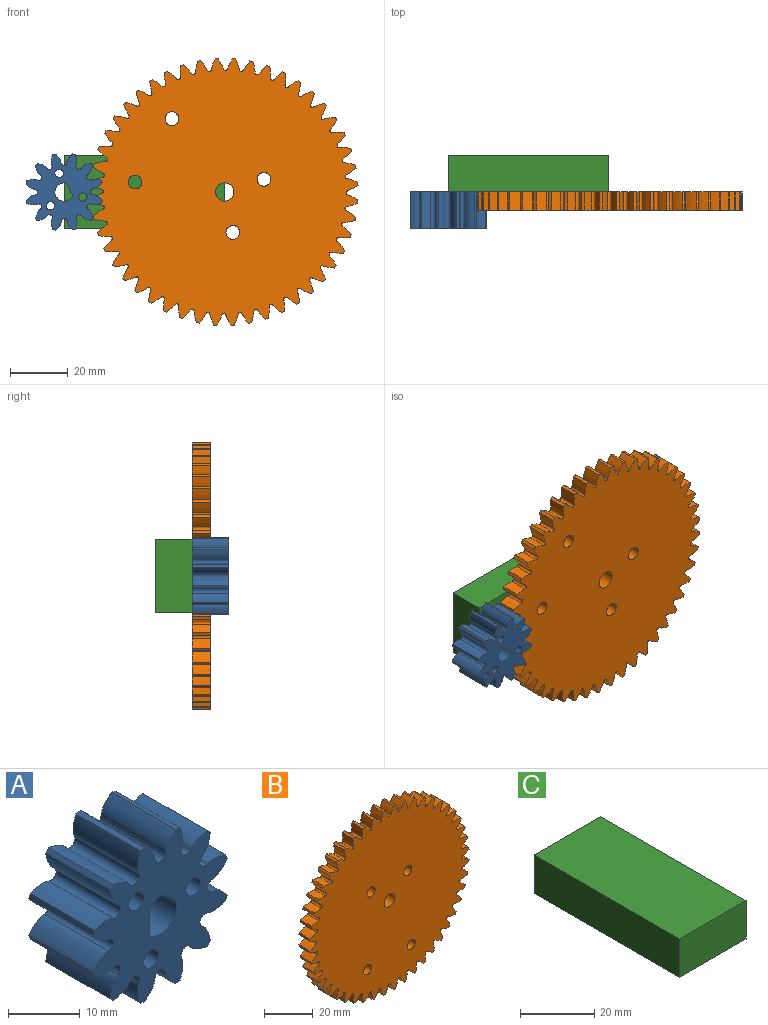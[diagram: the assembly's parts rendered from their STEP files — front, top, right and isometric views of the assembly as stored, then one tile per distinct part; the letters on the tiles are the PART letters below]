
ASSEMBLY  parts=3 mates=2
PART A: 55 faces, bbox 26.4x12.7x26.4 mm
  f0: cylinder r=13.54mm len=12.7mm, axis (0,1,0), area 10.8mm2, adj f11,f12,f41,f48
  f1: cylinder r=13.54mm len=12.7mm, axis (0,1,0), area 10.8mm2, adj f11,f12,f45,f47
  f2: cylinder r=13.54mm len=12.7mm, axis (0,1,0), area 10.8mm2, adj f11,f12,f38,f42
  f3: cylinder r=13.54mm len=12.7mm, axis (0,1,0), area 10.8mm2, adj f11,f12,f35,f39
  f4: cylinder r=13.54mm len=12.7mm, axis (0,1,0), area 10.8mm2, adj f11,f12,f32,f36
  f5: cylinder r=13.54mm len=12.7mm, axis (0,1,0), area 10.8mm2, adj f11,f12,f26,f33
  f6: cylinder r=13.54mm len=12.7mm, axis (0,1,0), area 10.8mm2, adj f11,f12,f14,f30
  f7: cylinder r=13.54mm len=12.7mm, axis (0,1,0), area 10.8mm2, adj f11,f12,f27,f29
  f8: cylinder r=13.54mm len=12.7mm, axis (0,1,0), area 10.8mm2, adj f11,f12,f20,f24
  f9: cylinder r=13.54mm len=12.7mm, axis (0,1,0), area 10.8mm2, adj f11,f12,f17,f21
  f10: cylinder r=13.54mm len=12.7mm, axis (0,1,0), area 10.8mm2, adj f11,f12,f18,f44
  f11: plane 26.38x26.38mm, normal (0,-1,0), area 363.7mm2, adj f0,f1,f2,f3,f4,f5,f6,f7
  f12: plane 26.38x26.38mm, normal (0,1,0), area 363.7mm2, adj f0,f1,f2,f3,f4,f5,f6,f7
  f13: cylinder r=13.54mm len=12.7mm, axis (0,1,0), area 10.8mm2, adj f11,f12,f15,f23
  f14: extruded ~12.7x3.07mm, area 48.5mm2, adj f6,f11,f12,f16
  f15: extruded ~12.7x3.07mm, area 48.5mm2, adj f11,f12,f13,f16
  f16: cylinder r=1.03mm len=12.7mm, axis (0,1,0), area 38.3mm2, adj f11,f12,f14,f15
  f17: extruded ~12.7x3.07mm, area 48.5mm2, adj f9,f11,f12,f19
  f18: extruded ~12.7x3.07mm, area 48.5mm2, adj f10,f11,f12,f19
  f19: cylinder r=1.03mm len=12.7mm, axis (0,1,0), area 38.3mm2, adj f11,f12,f17,f18
  f20: extruded ~12.7x3.33mm, area 48.5mm2, adj f8,f11,f12,f22
  f21: extruded ~12.7x3.69mm, area 48.5mm2, adj f9,f11,f12,f22
  f22: cylinder r=1.03mm len=12.7mm, axis (0,1,0), area 38.3mm2, adj f11,f12,f20,f21
  f23: extruded ~12.7x3.69mm, area 48.5mm2, adj f11,f12,f13,f25
  f24: extruded ~12.7x3.33mm, area 48.5mm2, adj f8,f11,f12,f25
  f25: cylinder r=1.03mm len=12.7mm, axis (0,1,0), area 38.3mm2, adj f11,f12,f23,f24
  f26: extruded ~12.7x3.69mm, area 48.5mm2, adj f5,f11,f12,f28
  f27: extruded ~12.7x3.33mm, area 48.5mm2, adj f7,f11,f12,f28
  f28: cylinder r=1.03mm len=12.7mm, axis (0,1,0), area 38.3mm2, adj f11,f12,f26,f27
  f29: extruded ~12.7x3.33mm, area 48.5mm2, adj f7,f11,f12,f31
  f30: extruded ~12.7x3.69mm, area 48.5mm2, adj f6,f11,f12,f31
  f31: cylinder r=1.03mm len=12.7mm, axis (0,1,0), area 38.3mm2, adj f11,f12,f29,f30
  f32: extruded ~12.7x3.07mm, area 48.5mm2, adj f4,f11,f12,f34
  f33: extruded ~12.7x3.07mm, area 48.5mm2, adj f5,f11,f12,f34
  f34: cylinder r=1.03mm len=12.7mm, axis (0,1,0), area 38.3mm2, adj f11,f12,f32,f33
  f35: extruded ~12.7x3.33mm, area 48.5mm2, adj f3,f11,f12,f37
  f36: extruded ~12.7x3.69mm, area 48.5mm2, adj f4,f11,f12,f37
  f37: cylinder r=1.03mm len=12.7mm, axis (0,1,0), area 38.3mm2, adj f11,f12,f35,f36
  f38: extruded ~12.7x3.69mm, area 48.5mm2, adj f2,f11,f12,f40
  f39: extruded ~12.7x3.33mm, area 48.5mm2, adj f3,f11,f12,f40
  f40: cylinder r=1.03mm len=12.7mm, axis (0,1,0), area 38.3mm2, adj f11,f12,f38,f39
  f41: extruded ~12.7x3.07mm, area 48.5mm2, adj f0,f11,f12,f43
  f42: extruded ~12.7x3.07mm, area 48.5mm2, adj f2,f11,f12,f43
  f43: cylinder r=1.03mm len=12.7mm, axis (0,1,0), area 38.3mm2, adj f11,f12,f41,f42
  f44: extruded ~12.7x3.69mm, area 48.5mm2, adj f10,f11,f12,f46
  f45: extruded ~12.7x3.33mm, area 48.5mm2, adj f1,f11,f12,f46
  f46: cylinder r=1.03mm len=12.7mm, axis (0,1,0), area 38.3mm2, adj f11,f12,f44,f45
  f47: extruded ~12.7x3.33mm, area 48.5mm2, adj f1,f11,f12,f49
  f48: extruded ~12.7x3.69mm, area 48.5mm2, adj f0,f11,f12,f49
  f49: cylinder r=1.03mm len=12.7mm, axis (0,1,0), area 38.3mm2, adj f11,f12,f47,f48
  f50: cylinder r=1.46mm len=12.7mm, axis (0,-1,0), area 116.5mm2, adj f11,f12
  f51: cylinder r=1.46mm len=12.7mm, axis (0,-1,0), area 116.5mm2, adj f11,f12
  f52: cylinder r=3.17mm len=12.7mm, axis (0,-1,0), area 183.5mm2, adj f11,f12,f53
  f53: plane 12.7x4.84mm, normal (1,0,0), area 61.4mm2, adj f11,f12,f52
  f54: cylinder r=1.46mm len=12.7mm, axis (0,-1,0), area 116.5mm2, adj f11,f12
PART B: 199 faces, bbox 92.4x6.4x92.4 mm
  f0: cylinder r=46.25mm len=6.35mm, axis (0,1,0), area 6.8mm2, adj f47,f48,f188,f192
  f1: cylinder r=46.25mm len=6.35mm, axis (0,1,0), area 6.8mm2, adj f47,f48,f179,f189
  f2: cylinder r=46.25mm len=6.35mm, axis (0,1,0), area 6.8mm2, adj f47,f48,f186,f191
  f3: cylinder r=46.25mm len=6.35mm, axis (0,1,0), area 6.8mm2, adj f47,f48,f183,f185
  f4: cylinder r=46.25mm len=6.35mm, axis (0,1,0), area 6.8mm2, adj f47,f48,f176,f180
  f5: cylinder r=46.25mm len=6.35mm, axis (0,1,0), area 6.8mm2, adj f47,f48,f173,f177
  f6: cylinder r=46.25mm len=6.35mm, axis (0,1,0), area 6.8mm2, adj f47,f48,f170,f174
  f7: cylinder r=46.25mm len=6.35mm, axis (0,1,0), area 6.8mm2, adj f47,f48,f167,f171
  f8: cylinder r=46.25mm len=6.35mm, axis (0,1,0), area 6.8mm2, adj f47,f48,f164,f168
  f9: cylinder r=46.25mm len=6.35mm, axis (0,1,0), area 6.8mm2, adj f47,f48,f161,f165
  f10: cylinder r=46.25mm len=6.35mm, axis (0,1,0), area 6.8mm2, adj f47,f48,f158,f162
  f11: cylinder r=46.25mm len=6.35mm, axis (0,1,0), area 6.8mm2, adj f47,f48,f146,f159
  f12: cylinder r=46.25mm len=6.35mm, axis (0,1,0), area 6.8mm2, adj f47,f48,f152,f156
  f13: cylinder r=46.25mm len=6.35mm, axis (0,1,0), area 6.8mm2, adj f47,f48,f143,f153
  f14: cylinder r=46.25mm len=6.35mm, axis (0,1,0), area 6.8mm2, adj f47,f48,f150,f155
  f15: cylinder r=46.25mm len=6.35mm, axis (0,1,0), area 6.8mm2, adj f47,f48,f147,f149
  f16: cylinder r=46.25mm len=6.35mm, axis (0,1,0), area 6.8mm2, adj f47,f48,f140,f144
  f17: cylinder r=46.25mm len=6.35mm, axis (0,1,0), area 6.8mm2, adj f47,f48,f137,f141
  f18: cylinder r=46.25mm len=6.35mm, axis (0,1,0), area 6.8mm2, adj f47,f48,f134,f138
  f19: cylinder r=46.25mm len=6.35mm, axis (0,1,0), area 6.8mm2, adj f47,f48,f131,f135
  f20: cylinder r=46.25mm len=6.35mm, axis (0,1,0), area 6.8mm2, adj f47,f48,f128,f132
  f21: cylinder r=46.25mm len=6.35mm, axis (0,1,0), area 6.8mm2, adj f47,f48,f125,f129
  f22: cylinder r=46.25mm len=6.35mm, axis (0,1,0), area 6.8mm2, adj f47,f48,f122,f126
  f23: cylinder r=46.25mm len=6.35mm, axis (0,1,0), area 6.8mm2, adj f47,f48,f110,f123
  f24: cylinder r=46.25mm len=6.35mm, axis (0,1,0), area 6.8mm2, adj f47,f48,f116,f120
  f25: cylinder r=46.25mm len=6.35mm, axis (0,1,0), area 6.8mm2, adj f47,f48,f107,f117
  f26: cylinder r=46.25mm len=6.35mm, axis (0,1,0), area 6.8mm2, adj f47,f48,f114,f119
  f27: cylinder r=46.25mm len=6.35mm, axis (0,1,0), area 6.8mm2, adj f47,f48,f111,f113
  f28: cylinder r=46.25mm len=6.35mm, axis (0,1,0), area 6.8mm2, adj f47,f48,f104,f108
  f29: cylinder r=46.25mm len=6.35mm, axis (0,1,0), area 6.8mm2, adj f47,f48,f101,f105
  f30: cylinder r=46.25mm len=6.35mm, axis (0,1,0), area 6.8mm2, adj f47,f48,f98,f102
  f31: cylinder r=46.25mm len=6.35mm, axis (0,1,0), area 6.8mm2, adj f47,f48,f50,f99
  f32: cylinder r=46.25mm len=6.35mm, axis (0,1,0), area 6.8mm2, adj f47,f48,f96,f182
  f33: cylinder r=46.25mm len=6.35mm, axis (0,1,0), area 6.8mm2, adj f47,f48,f93,f95
  f34: cylinder r=46.25mm len=6.35mm, axis (0,1,0), area 6.8mm2, adj f47,f48,f90,f92
  f35: cylinder r=46.25mm len=6.35mm, axis (0,1,0), area 6.8mm2, adj f47,f48,f87,f89
  f36: cylinder r=46.25mm len=6.35mm, axis (0,1,0), area 6.8mm2, adj f47,f48,f84,f86
  f37: cylinder r=46.25mm len=6.35mm, axis (0,1,0), area 6.8mm2, adj f47,f48,f81,f83
  f38: cylinder r=46.25mm len=6.35mm, axis (0,1,0), area 6.8mm2, adj f47,f48,f78,f80
  f39: cylinder r=46.25mm len=6.35mm, axis (0,1,0), area 6.8mm2, adj f47,f48,f75,f77
  f40: cylinder r=46.25mm len=6.35mm, axis (0,1,0), area 6.8mm2, adj f47,f48,f68,f72
  f41: cylinder r=46.25mm len=6.35mm, axis (0,1,0), area 6.8mm2, adj f47,f48,f62,f69
  f42: cylinder r=46.25mm len=6.35mm, axis (0,1,0), area 6.8mm2, adj f47,f48,f66,f74
  f43: cylinder r=46.25mm len=6.35mm, axis (0,1,0), area 6.8mm2, adj f47,f48,f63,f65
  f44: cylinder r=46.25mm len=6.35mm, axis (0,1,0), area 6.8mm2, adj f47,f48,f60,f71
  f45: cylinder r=46.25mm len=6.35mm, axis (0,1,0), area 6.8mm2, adj f47,f48,f57,f59
  f46: cylinder r=46.25mm len=6.35mm, axis (0,1,0), area 6.8mm2, adj f47,f48,f54,f56
  f47: plane 92.36x92.36mm, normal (0,-1,0), area 6064.5mm2, adj f0,f1,f2,f3,f4,f5,f6,f7
  f48: plane 92.36x92.36mm, normal (0,1,0), area 6064.5mm2, adj f0,f1,f2,f3,f4,f5,f6,f7
  f49: cylinder r=46.25mm len=6.35mm, axis (0,1,0), area 6.8mm2, adj f47,f48,f51,f53
  f50: extruded ~6.35x3.63mm, area 25.9mm2, adj f31,f47,f48,f52
  f51: extruded ~6.35x3.63mm, area 25.9mm2, adj f47,f48,f49,f52
  f52: cylinder r=0.7mm len=6.35mm, axis (0,1,0), area 10.8mm2, adj f47,f48,f50,f51
  f53: extruded ~6.35x3.84mm, area 25.9mm2, adj f47,f48,f49,f55
  f54: extruded ~6.35x3.36mm, area 25.9mm2, adj f46,f47,f48,f55
  f55: cylinder r=0.7mm len=6.35mm, axis (0,1,0), area 10.8mm2, adj f47,f48,f53,f54
  f56: extruded ~6.35x3.99mm, area 25.9mm2, adj f46,f47,f48,f58
  f57: extruded ~6.35x3.04mm, area 25.9mm2, adj f45,f47,f48,f58
  f58: cylinder r=0.7mm len=6.35mm, axis (0,1,0), area 10.8mm2, adj f47,f48,f56,f57
  f59: extruded ~6.35x4.06mm, area 25.9mm2, adj f45,f47,f48,f61
  f60: extruded ~6.35x3.09mm, area 25.9mm2, adj f44,f47,f48,f61
  f61: cylinder r=0.7mm len=6.35mm, axis (0,1,0), area 10.8mm2, adj f47,f48,f59,f60
  f62: extruded ~6.35x3.87mm, area 25.9mm2, adj f41,f47,f48,f64
  f63: extruded ~6.35x3.87mm, area 25.9mm2, adj f43,f47,f48,f64
  f64: cylinder r=0.7mm len=6.35mm, axis (0,1,0), area 10.8mm2, adj f47,f48,f62,f63
  f65: extruded ~6.35x3.67mm, area 25.9mm2, adj f43,f47,f48,f67
  f66: extruded ~6.35x4mm, area 25.9mm2, adj f42,f47,f48,f67
  f67: cylinder r=0.7mm len=6.35mm, axis (0,1,0), area 10.8mm2, adj f47,f48,f65,f66
  f68: extruded ~6.35x4mm, area 25.9mm2, adj f40,f47,f48,f70
  f69: extruded ~6.35x3.67mm, area 25.9mm2, adj f41,f47,f48,f70
  f70: cylinder r=0.7mm len=6.35mm, axis (0,1,0), area 10.8mm2, adj f47,f48,f68,f69
  f71: extruded ~6.35x4.07mm, area 25.9mm2, adj f44,f47,f48,f73
  f72: extruded ~6.35x3.41mm, area 25.9mm2, adj f40,f47,f48,f73
  f73: cylinder r=0.7mm len=6.35mm, axis (0,1,0), area 10.8mm2, adj f47,f48,f71,f72
  f74: extruded ~6.35x3.41mm, area 25.9mm2, adj f42,f47,f48,f76
  f75: extruded ~6.35x4.07mm, area 25.9mm2, adj f39,f47,f48,f76
  f76: cylinder r=0.7mm len=6.35mm, axis (0,1,0), area 10.8mm2, adj f47,f48,f74,f75
  f77: extruded ~6.35x3.09mm, area 25.9mm2, adj f39,f47,f48,f79
  f78: extruded ~6.35x4.06mm, area 25.9mm2, adj f38,f47,f48,f79
  f79: cylinder r=0.7mm len=6.35mm, axis (0,1,0), area 10.8mm2, adj f47,f48,f77,f78
  f80: extruded ~6.35x3.04mm, area 25.9mm2, adj f38,f47,f48,f82
  f81: extruded ~6.35x3.99mm, area 25.9mm2, adj f37,f47,f48,f82
  f82: cylinder r=0.7mm len=6.35mm, axis (0,1,0), area 10.8mm2, adj f47,f48,f80,f81
  f83: extruded ~6.35x3.36mm, area 25.9mm2, adj f37,f47,f48,f85
  f84: extruded ~6.35x3.84mm, area 25.9mm2, adj f36,f47,f48,f85
  f85: cylinder r=0.7mm len=6.35mm, axis (0,1,0), area 10.8mm2, adj f47,f48,f83,f84
  f86: extruded ~6.35x3.63mm, area 25.9mm2, adj f36,f47,f48,f88
  f87: extruded ~6.35x3.63mm, area 25.9mm2, adj f35,f47,f48,f88
  f88: cylinder r=0.7mm len=6.35mm, axis (0,1,0), area 10.8mm2, adj f47,f48,f86,f87
  f89: extruded ~6.35x3.84mm, area 25.9mm2, adj f35,f47,f48,f91
  f90: extruded ~6.35x3.36mm, area 25.9mm2, adj f34,f47,f48,f91
  f91: cylinder r=0.7mm len=6.35mm, axis (0,1,0), area 10.8mm2, adj f47,f48,f89,f90
  f92: extruded ~6.35x3.99mm, area 25.9mm2, adj f34,f47,f48,f94
  f93: extruded ~6.35x3.04mm, area 25.9mm2, adj f33,f47,f48,f94
  f94: cylinder r=0.7mm len=6.35mm, axis (0,1,0), area 10.8mm2, adj f47,f48,f92,f93
  f95: extruded ~6.35x4.06mm, area 25.9mm2, adj f33,f47,f48,f97
  f96: extruded ~6.35x3.09mm, area 25.9mm2, adj f32,f47,f48,f97
  f97: cylinder r=0.7mm len=6.35mm, axis (0,1,0), area 10.8mm2, adj f47,f48,f95,f96
  f98: extruded ~6.35x3.36mm, area 25.9mm2, adj f30,f47,f48,f100
  f99: extruded ~6.35x3.84mm, area 25.9mm2, adj f31,f47,f48,f100
  f100: cylinder r=0.7mm len=6.35mm, axis (0,1,0), area 10.8mm2, adj f47,f48,f98,f99
  f101: extruded ~6.35x3.04mm, area 25.9mm2, adj f29,f47,f48,f103
  f102: extruded ~6.35x3.99mm, area 25.9mm2, adj f30,f47,f48,f103
  f103: cylinder r=0.7mm len=6.35mm, axis (0,1,0), area 10.8mm2, adj f47,f48,f101,f102
  f104: extruded ~6.35x3.09mm, area 25.9mm2, adj f28,f47,f48,f106
  f105: extruded ~6.35x4.06mm, area 25.9mm2, adj f29,f47,f48,f106
  f106: cylinder r=0.7mm len=6.35mm, axis (0,1,0), area 10.8mm2, adj f47,f48,f104,f105
  f107: extruded ~6.35x3.41mm, area 25.9mm2, adj f25,f47,f48,f109
  f108: extruded ~6.35x4.07mm, area 25.9mm2, adj f28,f47,f48,f109
  f109: cylinder r=0.7mm len=6.35mm, axis (0,1,0), area 10.8mm2, adj f47,f48,f107,f108
  f110: extruded ~6.35x4.07mm, area 25.9mm2, adj f23,f47,f48,f112
  f111: extruded ~6.35x3.41mm, area 25.9mm2, adj f27,f47,f48,f112
  f112: cylinder r=0.7mm len=6.35mm, axis (0,1,0), area 10.8mm2, adj f47,f48,f110,f111
  f113: extruded ~6.35x4mm, area 25.9mm2, adj f27,f47,f48,f115
  f114: extruded ~6.35x3.67mm, area 25.9mm2, adj f26,f47,f48,f115
  f115: cylinder r=0.7mm len=6.35mm, axis (0,1,0), area 10.8mm2, adj f47,f48,f113,f114
  f116: extruded ~6.35x3.67mm, area 25.9mm2, adj f24,f47,f48,f118
  f117: extruded ~6.35x4mm, area 25.9mm2, adj f25,f47,f48,f118
  f118: cylinder r=0.7mm len=6.35mm, axis (0,1,0), area 10.8mm2, adj f47,f48,f116,f117
  f119: extruded ~6.35x3.87mm, area 25.9mm2, adj f26,f47,f48,f121
  f120: extruded ~6.35x3.87mm, area 25.9mm2, adj f24,f47,f48,f121
  f121: cylinder r=0.7mm len=6.35mm, axis (0,1,0), area 10.8mm2, adj f47,f48,f119,f120
  f122: extruded ~6.35x4.06mm, area 25.9mm2, adj f22,f47,f48,f124
  f123: extruded ~6.35x3.09mm, area 25.9mm2, adj f23,f47,f48,f124
  f124: cylinder r=0.7mm len=6.35mm, axis (0,1,0), area 10.8mm2, adj f47,f48,f122,f123
  f125: extruded ~6.35x3.99mm, area 25.9mm2, adj f21,f47,f48,f127
  f126: extruded ~6.35x3.04mm, area 25.9mm2, adj f22,f47,f48,f127
  f127: cylinder r=0.7mm len=6.35mm, axis (0,1,0), area 10.8mm2, adj f47,f48,f125,f126
  f128: extruded ~6.35x3.84mm, area 25.9mm2, adj f20,f47,f48,f130
  f129: extruded ~6.35x3.36mm, area 25.9mm2, adj f21,f47,f48,f130
  f130: cylinder r=0.7mm len=6.35mm, axis (0,1,0), area 10.8mm2, adj f47,f48,f128,f129
  f131: extruded ~6.35x3.63mm, area 25.9mm2, adj f19,f47,f48,f133
  f132: extruded ~6.35x3.63mm, area 25.9mm2, adj f20,f47,f48,f133
  f133: cylinder r=0.7mm len=6.35mm, axis (0,1,0), area 10.8mm2, adj f47,f48,f131,f132
  f134: extruded ~6.35x3.36mm, area 25.9mm2, adj f18,f47,f48,f136
  f135: extruded ~6.35x3.84mm, area 25.9mm2, adj f19,f47,f48,f136
  f136: cylinder r=0.7mm len=6.35mm, axis (0,1,0), area 10.8mm2, adj f47,f48,f134,f135
  f137: extruded ~6.35x3.04mm, area 25.9mm2, adj f17,f47,f48,f139
  f138: extruded ~6.35x3.99mm, area 25.9mm2, adj f18,f47,f48,f139
  f139: cylinder r=0.7mm len=6.35mm, axis (0,1,0), area 10.8mm2, adj f47,f48,f137,f138
  f140: extruded ~6.35x3.09mm, area 25.9mm2, adj f16,f47,f48,f142
  f141: extruded ~6.35x4.06mm, area 25.9mm2, adj f17,f47,f48,f142
  f142: cylinder r=0.7mm len=6.35mm, axis (0,1,0), area 10.8mm2, adj f47,f48,f140,f141
  f143: extruded ~6.35x3.41mm, area 25.9mm2, adj f13,f47,f48,f145
  f144: extruded ~6.35x4.07mm, area 25.9mm2, adj f16,f47,f48,f145
  f145: cylinder r=0.7mm len=6.35mm, axis (0,1,0), area 10.8mm2, adj f47,f48,f143,f144
  f146: extruded ~6.35x4.07mm, area 25.9mm2, adj f11,f47,f48,f148
  f147: extruded ~6.35x3.41mm, area 25.9mm2, adj f15,f47,f48,f148
  f148: cylinder r=0.7mm len=6.35mm, axis (0,1,0), area 10.8mm2, adj f47,f48,f146,f147
  f149: extruded ~6.35x4mm, area 25.9mm2, adj f15,f47,f48,f151
  f150: extruded ~6.35x3.67mm, area 25.9mm2, adj f14,f47,f48,f151
  f151: cylinder r=0.7mm len=6.35mm, axis (0,1,0), area 10.8mm2, adj f47,f48,f149,f150
  f152: extruded ~6.35x3.67mm, area 25.9mm2, adj f12,f47,f48,f154
  f153: extruded ~6.35x4mm, area 25.9mm2, adj f13,f47,f48,f154
  f154: cylinder r=0.7mm len=6.35mm, axis (0,1,0), area 10.8mm2, adj f47,f48,f152,f153
  f155: extruded ~6.35x3.87mm, area 25.9mm2, adj f14,f47,f48,f157
  f156: extruded ~6.35x3.87mm, area 25.9mm2, adj f12,f47,f48,f157
  f157: cylinder r=0.7mm len=6.35mm, axis (0,1,0), area 10.8mm2, adj f47,f48,f155,f156
  f158: extruded ~6.35x4.06mm, area 25.9mm2, adj f10,f47,f48,f160
  f159: extruded ~6.35x3.09mm, area 25.9mm2, adj f11,f47,f48,f160
  f160: cylinder r=0.7mm len=6.35mm, axis (0,1,0), area 10.8mm2, adj f47,f48,f158,f159
  f161: extruded ~6.35x3.99mm, area 25.9mm2, adj f9,f47,f48,f163
  f162: extruded ~6.35x3.04mm, area 25.9mm2, adj f10,f47,f48,f163
  f163: cylinder r=0.7mm len=6.35mm, axis (0,1,0), area 10.8mm2, adj f47,f48,f161,f162
  f164: extruded ~6.35x3.84mm, area 25.9mm2, adj f8,f47,f48,f166
  f165: extruded ~6.35x3.36mm, area 25.9mm2, adj f9,f47,f48,f166
  f166: cylinder r=0.7mm len=6.35mm, axis (0,1,0), area 10.8mm2, adj f47,f48,f164,f165
  f167: extruded ~6.35x3.63mm, area 25.9mm2, adj f7,f47,f48,f169
  f168: extruded ~6.35x3.63mm, area 25.9mm2, adj f8,f47,f48,f169
  f169: cylinder r=0.7mm len=6.35mm, axis (0,1,0), area 10.8mm2, adj f47,f48,f167,f168
  f170: extruded ~6.35x3.36mm, area 25.9mm2, adj f6,f47,f48,f172
  f171: extruded ~6.35x3.84mm, area 25.9mm2, adj f7,f47,f48,f172
  f172: cylinder r=0.7mm len=6.35mm, axis (0,1,0), area 10.8mm2, adj f47,f48,f170,f171
  f173: extruded ~6.35x3.04mm, area 25.9mm2, adj f5,f47,f48,f175
  f174: extruded ~6.35x3.99mm, area 25.9mm2, adj f6,f47,f48,f175
  f175: cylinder r=0.7mm len=6.35mm, axis (0,1,0), area 10.8mm2, adj f47,f48,f173,f174
  f176: extruded ~6.35x3.09mm, area 25.9mm2, adj f4,f47,f48,f178
  f177: extruded ~6.35x4.06mm, area 25.9mm2, adj f5,f47,f48,f178
  f178: cylinder r=0.7mm len=6.35mm, axis (0,1,0), area 10.8mm2, adj f47,f48,f176,f177
  f179: extruded ~6.35x3.41mm, area 25.9mm2, adj f1,f47,f48,f181
  f180: extruded ~6.35x4.07mm, area 25.9mm2, adj f4,f47,f48,f181
  f181: cylinder r=0.7mm len=6.35mm, axis (0,1,0), area 10.8mm2, adj f47,f48,f179,f180
  f182: extruded ~6.35x4.07mm, area 25.9mm2, adj f32,f47,f48,f184
  f183: extruded ~6.35x3.41mm, area 25.9mm2, adj f3,f47,f48,f184
  f184: cylinder r=0.7mm len=6.35mm, axis (0,1,0), area 10.8mm2, adj f47,f48,f182,f183
  f185: extruded ~6.35x4mm, area 25.9mm2, adj f3,f47,f48,f187
  f186: extruded ~6.35x3.67mm, area 25.9mm2, adj f2,f47,f48,f187
  f187: cylinder r=0.7mm len=6.35mm, axis (0,1,0), area 10.8mm2, adj f47,f48,f185,f186
  f188: extruded ~6.35x3.67mm, area 25.9mm2, adj f0,f47,f48,f190
  f189: extruded ~6.35x4mm, area 25.9mm2, adj f1,f47,f48,f190
  f190: cylinder r=0.7mm len=6.35mm, axis (0,1,0), area 10.8mm2, adj f47,f48,f188,f189
  f191: extruded ~6.35x3.87mm, area 25.9mm2, adj f2,f47,f48,f193
  f192: extruded ~6.35x3.87mm, area 25.9mm2, adj f0,f47,f48,f193
  f193: cylinder r=0.7mm len=6.35mm, axis (0,1,0), area 10.8mm2, adj f47,f48,f191,f192
  f194: cylinder r=2.39mm len=6.35mm, axis (0,-1,0), area 95.3mm2, adj f47,f48
  f195: cylinder r=2.39mm len=6.35mm, axis (0,-1,0), area 95.3mm2, adj f47,f48
  f196: cylinder r=2.39mm len=6.35mm, axis (0,-1,0), area 95.3mm2, adj f47,f48
  f197: cylinder r=2.39mm len=6.35mm, axis (0,-1,0), area 95.3mm2, adj f47,f48
  f198: cylinder r=3.17mm len=6.35mm, axis (0,-1,0), area 126.7mm2, adj f47,f48
PART C: 6 faces, bbox 25.4x55.6x12.7 mm
  f0: plane 25.4x12.7mm, normal (0,1,0), area 322.6mm2, adj f1,f3,f4,f5
  f1: plane 55.63x12.7mm, normal (-1,0,0), area 706.5mm2, adj f0,f2,f4,f5
  f2: plane 25.4x12.7mm, normal (0,-1,0), area 322.6mm2, adj f1,f3,f4,f5
  f3: plane 55.63x12.7mm, normal (1,0,0), area 706.5mm2, adj f0,f2,f4,f5
  f4: plane 55.63x25.4mm, normal (0,0,1), area 1412.9mm2, adj f0,f1,f2,f3
  f5: plane 55.63x25.4mm, normal (0,0,-1), area 1412.9mm2, adj f0,f1,f2,f3
PLACE A rot(axis=(0,1,0),149.7deg) t=(-27.81,0,0)mm
PLACE B rot(axis=(0,1,0),120.3deg) t=(27.81,0,0)mm
PLACE C rot(axis=(-0.58,-0.58,-0.58),120deg) t=(-27.81,0,-12.7)mm
MATE cylindrical A.f0 <-> C.f5  axis (0,1,0) through (-27.81,0,0)mm
MATE cylindrical B.f0 <-> C.f5  axis (0,1,0) through (27.81,0,0)mm
